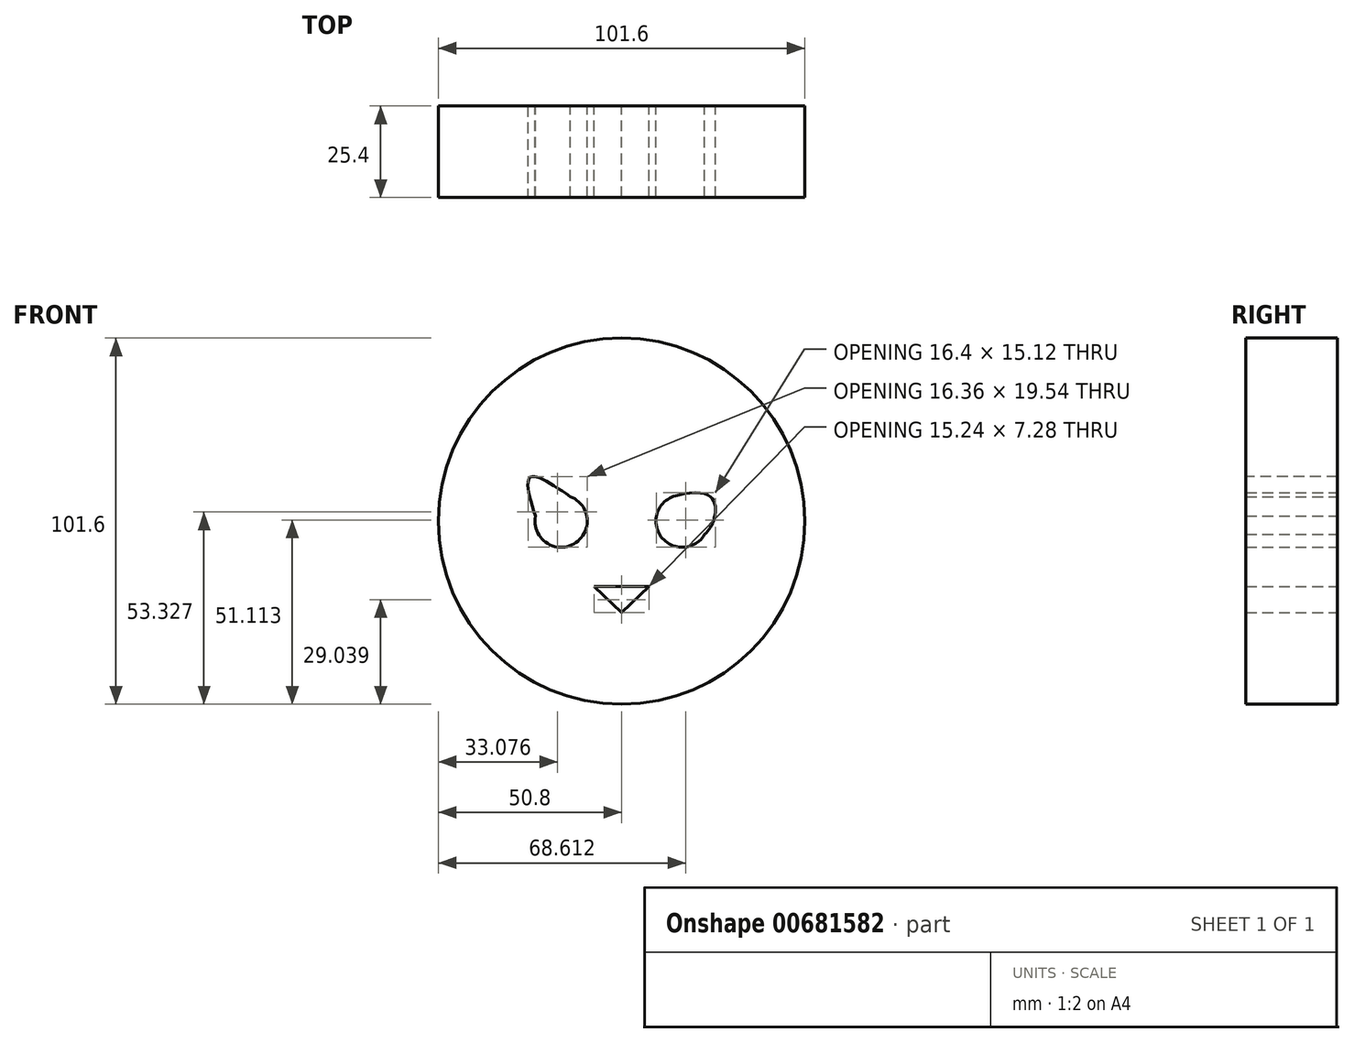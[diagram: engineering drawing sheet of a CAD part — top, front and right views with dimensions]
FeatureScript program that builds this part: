
annotation { "Feature Type Name" : "Feature", "Feature Type Description" : "" }
export const myFeature = defineFeature(function(context is Context, id is Id, definition is map)
    precondition{}
    {
        {
            var Q0;
            Q0=qCreatedBy(makeId("Front.planeOp"),FACE);
            var sketch = newSketch(context, id + "F0", { "sketchPlane" : qUnion([Q0])});
            skCircle(sketch, "E0", {"center": v(0, 0) * mm, "radius": 50.8 * mm});
            skLineSegment(sketch, "E1", {"start": v(0, 50.8) * mm, "end": v(0, -50.8) * mm, "construction": true});
            skCircle(sketch, "E2", {"center": v(-16.78, 0) * mm, "radius": 7.26 * mm});
            skCircle(sketch, "E3", {"center": v(16.78, 0) * mm, "radius": 7.26 * mm});
            skLineSegment(sketch, "E4", {"start": v(-16.78, 0) * mm, "end": v(16.78, 0) * mm, "construction": true});
            skLineSegment(sketch, "E5", {"start": v(-7.62, -18.12) * mm, "end": v(7.62, -18.12) * mm});
            skLineSegment(sketch, "E6", {"start": v(7.62, -18.12) * mm, "end": v(0, -25.4) * mm});
            skLineSegment(sketch, "E7", {"start": v(0, -25.4) * mm, "end": v(-7.62, -18.12) * mm});
            skPoint(sketch, "E8", {"position": v(0, -18.12) * mm});
            skLineSegment(sketch, "E9", {"start": v(-44, -25.4) * mm, "end": v(44, -25.4) * mm, "construction": true});
            skLineSegment(sketch, "E10", {"start": v(44, -25.4) * mm, "end": v(44, 25.4) * mm, "construction": true});
            skLineSegment(sketch, "E11", {"start": v(44, 25.4) * mm, "end": v(-44, 25.4) * mm, "construction": true});
            skLineSegment(sketch, "E12", {"start": v(-44, 25.4) * mm, "end": v(-44, -25.4) * mm, "construction": true});
            skLineSegment(sketch, "E13", {"start": v(-25.4, 44) * mm, "end": v(-25.4, -44) * mm, "construction": true});
            skLineSegment(sketch, "E14", {"start": v(-25.4, -44) * mm, "end": v(25.4, -44) * mm, "construction": true});
            skLineSegment(sketch, "E15", {"start": v(25.4, -44) * mm, "end": v(25.4, 44) * mm, "construction": true});
            skLineSegment(sketch, "E16", {"start": v(25.4, 44) * mm, "end": v(-25.4, 44) * mm, "construction": true});
            skLineSegment(sketch, "E17", {"start": v(-50.8, 0) * mm, "end": v(50.8, 0) * mm, "construction": true});
            skPoint(sketch, "E17.endSnap0", {"position": v(44, 0) * mm});
            skLineSegment(sketch, "E18", {"start": v(9.52, 0) * mm, "end": v(7.62, -18.12) * mm, "construction": true});
            skLineSegment(sketch, "E19", {"start": v(-7.62, -18.12) * mm, "end": v(-9.49, 0) * mm, "construction": true});
            skFitSpline(sketch, "E20", {"points": [v(14.95, 7.02) * mm, v(25.4, 0) * mm, v(14.84, -7) * mm], "startDerivative": vector(72.75, 18.95) * mm, "endDerivative": vector(-41.83, -10.61) * mm});
            skFitSpline(sketch, "E21", {"points": [v(-14.26, 6.8) * mm, v(-25.4, 12.1) * mm, v(-21.48, -5.54) * mm], "startDerivative": vector(-31.83, 21.63) * mm, "endDerivative": vector(15.88, -44.23) * mm});
            skSolve(sketch);
        }
        {
            var Q0;
            Q0=makeQuery(id+"F0.imprint","IMPRINT",FACE,{"disambiguationData":[TD([[makeQuery(id+"F0.imprint","IMPRINT",EDGE,{"derivedFrom":sQuery(id+"F0.wireOp",EDGE,"E0")}),1.0]])]});
            extrude(context, id + "F1", {"entities" : qUnion([Q0]), "depth" : 25.4 * mm, "offsetDistance" : 25.4 * mm});
        }
    });
